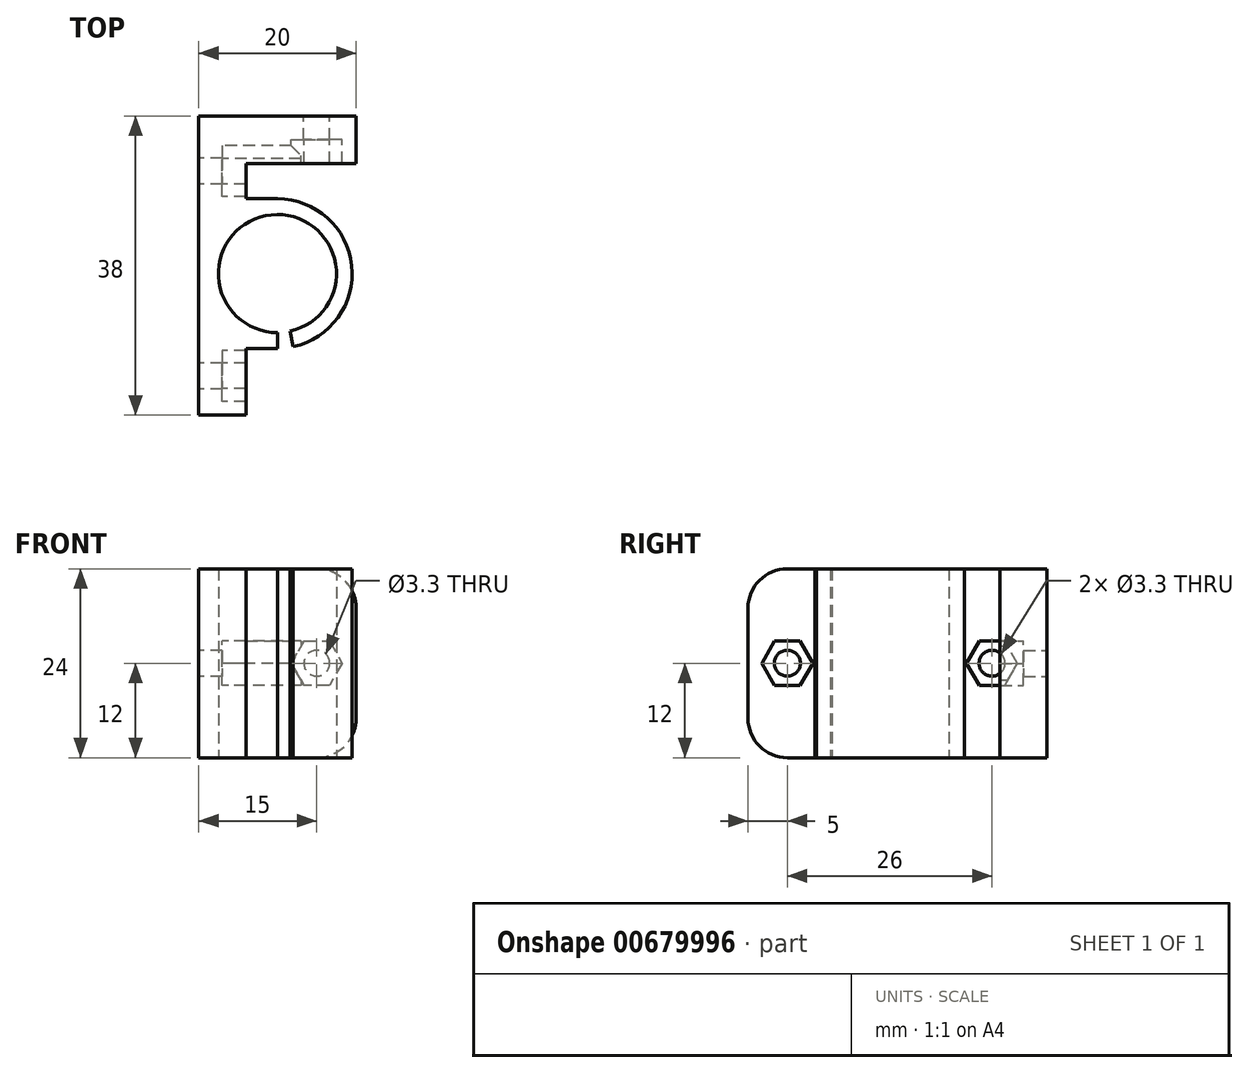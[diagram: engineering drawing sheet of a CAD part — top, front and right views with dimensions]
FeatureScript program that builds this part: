
annotation { "Feature Type Name" : "Feature", "Feature Type Description" : "" }
export const myFeature = defineFeature(function(context is Context, id is Id, definition is map)
    precondition{}
    {
        {
            var Q0;
            Q0=qCreatedBy(makeId("Top.planeOp"),FACE);
            var sketch = newSketch(context, id + "F0", { "sketchPlane" : qUnion([Q0])});
            skLineSegment(sketch, "E0", {"start": v(0, 0) * mm, "end": v(20, 0) * mm});
            skLineSegment(sketch, "E1", {"start": v(0, 0) * mm, "end": v(0, -38) * mm});
            skLineSegment(sketch, "E2", {"start": v(0, -38) * mm, "end": v(6, -38) * mm});
            skCircle(sketch, "E3", {"center": v(10, -20) * mm, "radius": 9.5 * mm});
            skCircle(sketch, "E4", {"center": v(10, -20) * mm, "radius": 7.5 * mm});
            skLineSegment(sketch, "E5", {"start": v(6, -38) * mm, "end": v(6, -28.62) * mm});
            skLineSegment(sketch, "E6", {"start": v(20, 0) * mm, "end": v(20, -6) * mm});
            skLineSegment(sketch, "E7", {"start": v(20, -6) * mm, "end": v(6, -6) * mm});
            skLineSegment(sketch, "E8", {"start": v(6, -6) * mm, "end": v(6, -11.38) * mm});
            skLineSegment(sketch, "E9", {"start": v(6, -11.38) * mm, "end": v(6, -28.62) * mm, "construction": true});
            skLineSegment(sketch, "E10", {"start": v(10, -10.5) * mm, "end": v(6, -10.5) * mm});
            skLineSegment(sketch, "E11", {"start": v(10, -29.5) * mm, "end": v(6, -29.5) * mm});
            skLineSegment(sketch, "E12", {"start": v(10, -29.5) * mm, "end": v(10, -27.5) * mm});
            skLineSegment(sketch, "E13", {"start": v(10, -27.5) * mm, "end": v(10, -20) * mm});
            skLineSegment(sketch, "E14", {"start": v(12, -29.29) * mm, "end": v(10, -20) * mm});
            skPoint(sketch, "E15", {"position": v(11.58, -27.33) * mm});
            skSolve(sketch);
        }
        {
            var Q0;
            Q0=makeQuery(id+"F0.imprint","IMPRINT",FACE,{"disambiguationData":[TD([[makeQuery(id+"F0.imprint","IMPRINT",EDGE,{"derivedFrom":sQuery(id+"F0.wireOp",EDGE,"E0")}),-1.0]])]});
            var Q1;
            {var subQ5=sQuery(id+"F0.wireOp",EDGE,"E12");Q1=makeQuery(id+"F0.imprint","IMPRINT",FACE,{"disambiguationData":[TD([[makeQuery(id+"F0.imprint","IMPRINT",EDGE,{"derivedFrom":subQ5}),1.0]])]});}
            var Q2;
            {var subQ0=sQuery(id+"F0.wireOp",EDGE,"E11");Q2=makeQuery(id+"F0.imprint","IMPRINT",FACE,{"disambiguationData":[TD([[makeQuery(id+"F0.imprint","IMPRINT",EDGE,{"derivedFrom":subQ0}),-1.0]])]});}
            var Q3;
            {var subQ0=sQuery(id+"F0.wireOp",EDGE,"E10");Q3=makeQuery(id+"F0.imprint","IMPRINT",FACE,{"disambiguationData":[TD([[makeQuery(id+"F0.imprint","IMPRINT",EDGE,{"derivedFrom":subQ0}),1.0]])]});}
            extrude(context, id + "F1", {"entities" : qUnion([Q0, Q1, Q2, Q3]), "depth" : 24 * mm});
        }
        {
            var Q0;
            Q0=makeQuery(id+"F1.opExtrude","SWEPT_FACE",FACE,{"disambiguationData":[OSD([sQuery(id+"F0.wireOp",EDGE,"E1")])]});
            cPlane(context, id + "F2", {"entities" : qUnion([Q0]), "cplaneType" : CPlaneType.OFFSET, "offset" : 3 * mm, "oppositeDirection" : true, "width" : 150 * mm, "height" : 150 * mm});
        }
        {
            var Q0;
            Q0=qCreatedBy(id+"F2.planeOp",FACE);
            var sketch = newSketch(context, id + "F3", { "sketchPlane" : qUnion([Q0])});
            skLineSegment(sketch, "E16", {"start": v(7, 12) * mm, "end": v(20, 12) * mm, "construction": true});
            skLineSegment(sketch, "E17", {"start": v(20, 12) * mm, "end": v(33, 12) * mm, "construction": true});
            skCircle(sketch, "E18", {"center": v(7, 12) * mm, "radius": 1.65 * mm});
            skCircle(sketch, "E19", {"center": v(33, 12) * mm, "radius": 1.65 * mm});
            skCircle(sketch, "E20.cCircle", {"center": v(7, 12) * mm, "radius": 2.8 * mm, "construction": true});
            skLineSegment(sketch, "E20.0", {"start": v(5.38, 14.8) * mm, "end": v(8.62, 14.8) * mm});
            skLineSegment(sketch, "E20.1", {"start": v(8.62, 14.8) * mm, "end": v(10.23, 12) * mm});
            skLineSegment(sketch, "E20.2", {"start": v(10.23, 12) * mm, "end": v(8.62, 9.2) * mm});
            skLineSegment(sketch, "E20.3", {"start": v(8.62, 9.2) * mm, "end": v(5.38, 9.2) * mm});
            skLineSegment(sketch, "E20.4", {"start": v(5.38, 9.2) * mm, "end": v(3.77, 12) * mm});
            skLineSegment(sketch, "E20.5", {"start": v(3.77, 12) * mm, "end": v(5.38, 14.8) * mm});
            skPoint(sketch, "E20.0.midPoint", {"position": v(7, 14.8) * mm});
            skCircle(sketch, "E21.cCircle", {"center": v(33, 12) * mm, "radius": 2.8 * mm, "construction": true});
            skLineSegment(sketch, "E21.0", {"start": v(31.38, 14.8) * mm, "end": v(34.62, 14.8) * mm});
            skLineSegment(sketch, "E21.1", {"start": v(34.62, 14.8) * mm, "end": v(36.23, 12) * mm});
            skLineSegment(sketch, "E21.2", {"start": v(36.23, 12) * mm, "end": v(34.62, 9.2) * mm});
            skLineSegment(sketch, "E21.3", {"start": v(34.62, 9.2) * mm, "end": v(31.38, 9.2) * mm});
            skLineSegment(sketch, "E21.4", {"start": v(31.38, 9.2) * mm, "end": v(29.77, 12) * mm});
            skLineSegment(sketch, "E21.5", {"start": v(29.77, 12) * mm, "end": v(31.38, 14.8) * mm});
            skPoint(sketch, "E21.0.midPoint", {"position": v(33, 14.8) * mm});
            skSolve(sketch);
        }
        {
            var Q0;
            Q0=makeQuery(id+"F3.imprint","IMPRINT",FACE,{"disambiguationData":[TD([[makeQuery(id+"F3.imprint","IMPRINT",EDGE,{"derivedFrom":sQuery(id+"F3.wireOp",EDGE,"E18")}),1.0]])]});
            var Q1;
            Q1=makeQuery(id+"F3.imprint","IMPRINT",FACE,{"disambiguationData":[TD([[makeQuery(id+"F3.imprint","IMPRINT",EDGE,{"derivedFrom":sQuery(id+"F3.wireOp",EDGE,"E19")}),1.0]])]});
            extrude(context, id + "F4", {"entities" : qUnion([Q0, Q1]), "operationType" : NewBodyOperationType.REMOVE, "oppositeDirection" : true, "depth" : 10 * mm, "hasSecondDirection" : true, "secondDirectionBound" : SecondDirectionBoundingType.THROUGH_ALL, "secondDirectionOppositeDirection" : false, "secondDirectionDepth" : 25 * mm});
        }
        {
            var Q0;
            Q0=qSketchRegion(id+"F3",true);
            extrude(context, id + "F5", {"entities" : qUnion([Q0]), "operationType" : NewBodyOperationType.REMOVE, "oppositeDirection" : true, "depth" : 10 * mm});
        }
        {
            var Q0;
            Q0=makeQuery(id+"F1.opExtrude","SWEPT_FACE",FACE,{"disambiguationData":[OSD([sQuery(id+"F0.wireOp",EDGE,"E0")])]});
            cPlane(context, id + "F6", {"entities" : qUnion([Q0]), "cplaneType" : CPlaneType.OFFSET, "offset" : 3 * mm, "oppositeDirection" : true, "width" : 150 * mm, "height" : 150 * mm});
        }
        {
            var Q0;
            Q0=qCreatedBy(id+"F6.planeOp",FACE);
            var sketch = newSketch(context, id + "F7", { "sketchPlane" : qUnion([Q0])});
            skCircle(sketch, "E22", {"center": v(-15, 12) * mm, "radius": 1.65 * mm});
            skCircle(sketch, "E23.cCircle", {"center": v(-15, 12) * mm, "radius": 2.8 * mm, "construction": true});
            skLineSegment(sketch, "E23.0", {"start": v(-16.62, 14.8) * mm, "end": v(-13.38, 14.8) * mm});
            skLineSegment(sketch, "E23.1", {"start": v(-13.38, 14.8) * mm, "end": v(-11.77, 12) * mm});
            skLineSegment(sketch, "E23.2", {"start": v(-11.77, 12) * mm, "end": v(-13.38, 9.2) * mm});
            skLineSegment(sketch, "E23.3", {"start": v(-13.38, 9.2) * mm, "end": v(-16.62, 9.2) * mm});
            skLineSegment(sketch, "E23.4", {"start": v(-16.62, 9.2) * mm, "end": v(-18.23, 12) * mm});
            skLineSegment(sketch, "E23.5", {"start": v(-18.23, 12) * mm, "end": v(-16.62, 14.8) * mm});
            skPoint(sketch, "E23.0.midPoint", {"position": v(-15, 14.8) * mm});
            skSolve(sketch);
        }
        {
            var Q0;
            Q0=qSketchRegion(id+"F7",true);
            extrude(context, id + "F8", {"entities" : qUnion([Q0]), "operationType" : NewBodyOperationType.REMOVE, "oppositeDirection" : true, "depth" : 6 * mm});
        }
        {
            var Q0;
            Q0=makeQuery(id+"F7.imprint","IMPRINT",FACE,{"disambiguationData":[TD([[makeQuery(id+"F7.imprint","IMPRINT",EDGE,{"derivedFrom":sQuery(id+"F7.wireOp",EDGE,"E22")}),1.0]])]});
            extrude(context, id + "F9", {"entities" : qUnion([Q0]), "operationType" : NewBodyOperationType.REMOVE, "oppositeDirection" : true, "depth" : 7 * mm, "hasSecondDirection" : true, "secondDirectionBound" : SecondDirectionBoundingType.THROUGH_ALL, "secondDirectionOppositeDirection" : false, "secondDirectionDepth" : 25 * mm});
        }
        {
            var Q0;
            Q0=makeQuery(id+"F1.opExtrude","CAP_EDGE",EDGE,{"disambiguationData":[OSD([sQuery(id+"F0.wireOp",EDGE,"E2")])],"isStart":false});
            var Q1;
            Q1=makeQuery(id+"F1.opExtrude","CAP_EDGE",EDGE,{"disambiguationData":[OSD([sQuery(id+"F0.wireOp",EDGE,"E6")])],"isStart":false});
            var Q2;
            Q2=makeQuery(id+"F1.opExtrude","CAP_EDGE",EDGE,{"disambiguationData":[OSD([sQuery(id+"F0.wireOp",EDGE,"E6")])],"isStart":true});
            var Q3;
            Q3=makeQuery(id+"F1.opExtrude","CAP_EDGE",EDGE,{"disambiguationData":[OSD([sQuery(id+"F0.wireOp",EDGE,"E2")])],"isStart":true});
            fillet(context, id + "F10", {"entities" : qUnion([Q0, Q1, Q2, Q3]), "radius" : 5 * mm, "tangentPropagation" : true, "allowEdgeOverflow" : false});
        }
    });
